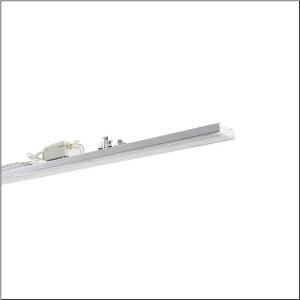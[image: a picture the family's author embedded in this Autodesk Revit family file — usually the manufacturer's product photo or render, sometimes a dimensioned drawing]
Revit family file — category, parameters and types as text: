
# Revit family: licross_r__21_recessed_ho_52tl1ede47xs_a4c3
name_source: partatom
category: Lighting Fixtures
units: mm (PartAtom-declared; Revit-internal decimal feet)

## family parameters
Cut with Voids When Loaded = No
Host = Face
Light Source = No
Part Type = Normal
Room Calculation Point = No
Round Connector Dimension = Use Diameter
Shared = No

## types (1)
- --- (1 x LED, 7310 lm, 44.1 W, 4000K)
    Apparent Load = 44 VA
    CIE Flux Codes = 85 95 99 100 100
    Color Rendering = 80
    Color Temperature = 4000K
    Default Elevation = 1800 mm
    Description = Licross® 21 Recessed HO, luminaire insert, of sheet steel, galvanised, coil coated, white, length: 750mm, width: 66mm, height: 67mm, LED rated luminous flux: 7.310lm, light colour: 840, control gear: DALI 2, with plug, 5-pole, with phase selection, mains connection: 220..240V, AC, 50/60Hz, rated input power: 44W, halogen-free wiring, primary light control with lens, of plastic, primary optical cover: cover, of PMMA, light emission: direct distribution, primary light characteristic: symmetric, protection rating (complete): IP40, insulation class (complete): insulation class I (protective earthing), certification: CE, ENEC, VDE, UKCA, protection symbol: D if used in an environment without relevant dust loads with corresponding accessories, impact resistance: IK06, permissible ambient temperature for indoor applications: -25..+30°C, corresponds to IFS (International Featured Standards) requirements for safety and quality in the food industry, reducing of maximum allowable ambient temperature of 5°C with ceiling mounting, LABS conformity tested according to VDMA 24364:2018-05, packaging unit: 1 piece
    Height = 58 mm
    Lamp = 1 x LED
    Lamp Light Flux = 7310 lm
    Lamp Power = 44.1 W
    Lamp count = 1
    Length = 750 mm
    Luminous efficacy = 166 lm/W
    Manufacturer = Siteco
    ModVariant = No
    Model = 52TL1EDE47XS
    Mounting Place = Ceiling
    Mounting Type = Pendant
    Number of Poles = 1
    OnlyDefault = Yes
    Power Factor = 1
    Product Name = Licross® 21 Recessed HO
    Product group = luminaire insert
    ProductGroupID = 901
    Protection Class = Protection class I
    Protection Degree = IP 40
    RLX_Detail_Level = 1
    RLX_Emergency_Light_Flux = 0 lm
    RLX_Emergency_Type = 0
    RLX_Emergency_Type_DB = No
    RlxData = <blob elided: 29413 chars, md5=1ba5bcb2>
    Socket = socket
    Standby Power = 0 W
    System Light Flux = 7310 lm
    System Power = 44 W
    Type Comments = factory setting: luminous flux: 100 % | dim-lin: 254 | 484 mA
    Type Image = l_1296930.jpg
    URL = http://relux.com
    VarID = @adj_057167
    Voltage = 0 V
    Weight = 0.00 kg
    Width = 66 mm

## geometry (parser evidence)
native form markers: Blend x4, Sweep x10
no freeform markers — native parametric forms only
